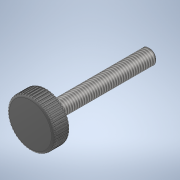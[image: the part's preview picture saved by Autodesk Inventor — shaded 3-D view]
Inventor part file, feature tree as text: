
AUTODESK INVENTOR PART (.ipt)
format: ipt  version: 2020 (Build 240168000, 168)  size: 434,176 bytes
history: native  units: mm
features: projected_geometry x5, extrude x4, sketch x4, fillet x2, chamfer x1, thread x1, pattern_circular x1
ambient origin geometry x8: Origin, YZ Plane, XZ Plane, XY Plane, X Axis, Y Axis, Z Axis, Center Point
bodies: Solid1 (feature_tree)
feature tree (18):
  extrude  "Extrusion1"  Depth=4.4mm TaperAngle=0.0deg
  extrude  "Extrusion2"  Depth=20.0mm TaperAngle=0.0deg
  extrude  "Extrusion3"  Depth=0.25mm TaperAngle=0.0deg
  chamfer  "Chamfer1"  Distance=0.25mm Angle=45.0deg
  fillet  "Fillet1"  Radius=0.5mm
  fillet  "Fillet2"  Radius=0.25mm
  thread  "Thread1"  [1 undecoded]
  extrude  "Extrusion4"  Depth=0.25mm
  pattern_circular  "Circular Pattern1"  [2 undecoded]
  sketch  "Sketch1"  dims[d0=9.6mm d1=4.4mm d2=0.0mm]
  sketch  "Sketch2"  dims[d3=3.0mm d4=20.0mm d5=0.0mm]
  sketch  "Sketch3"  dims[d7=6.0mm d8=1.0mm d9=0.0mm d10=0.25mm d11=2.0mm d12=45.0deg d13=0.5mm d14=0.25mm d15=19.75mm d16=0.0mm]
  sketch  "Sketch4"  dims[d17=0.25mm d18=0.125mm d19=0.0mm d20=0.0mm d21=500.0mm d22=360.0deg]
  projected_geometry  "Project Cut Edges1"
  projected_geometry  "Project Cut Edges2"
  projected_geometry  "Project Cut Edges3"
  projected_geometry  "Project Cut Edges4"
  projected_geometry  "Project Cut Edges5"
note: 3 required parameter values undecoded (feature->parameter linkage not recoverable at this tier; creation-order binding heuristic only, values carry confidence <= 0.55)
